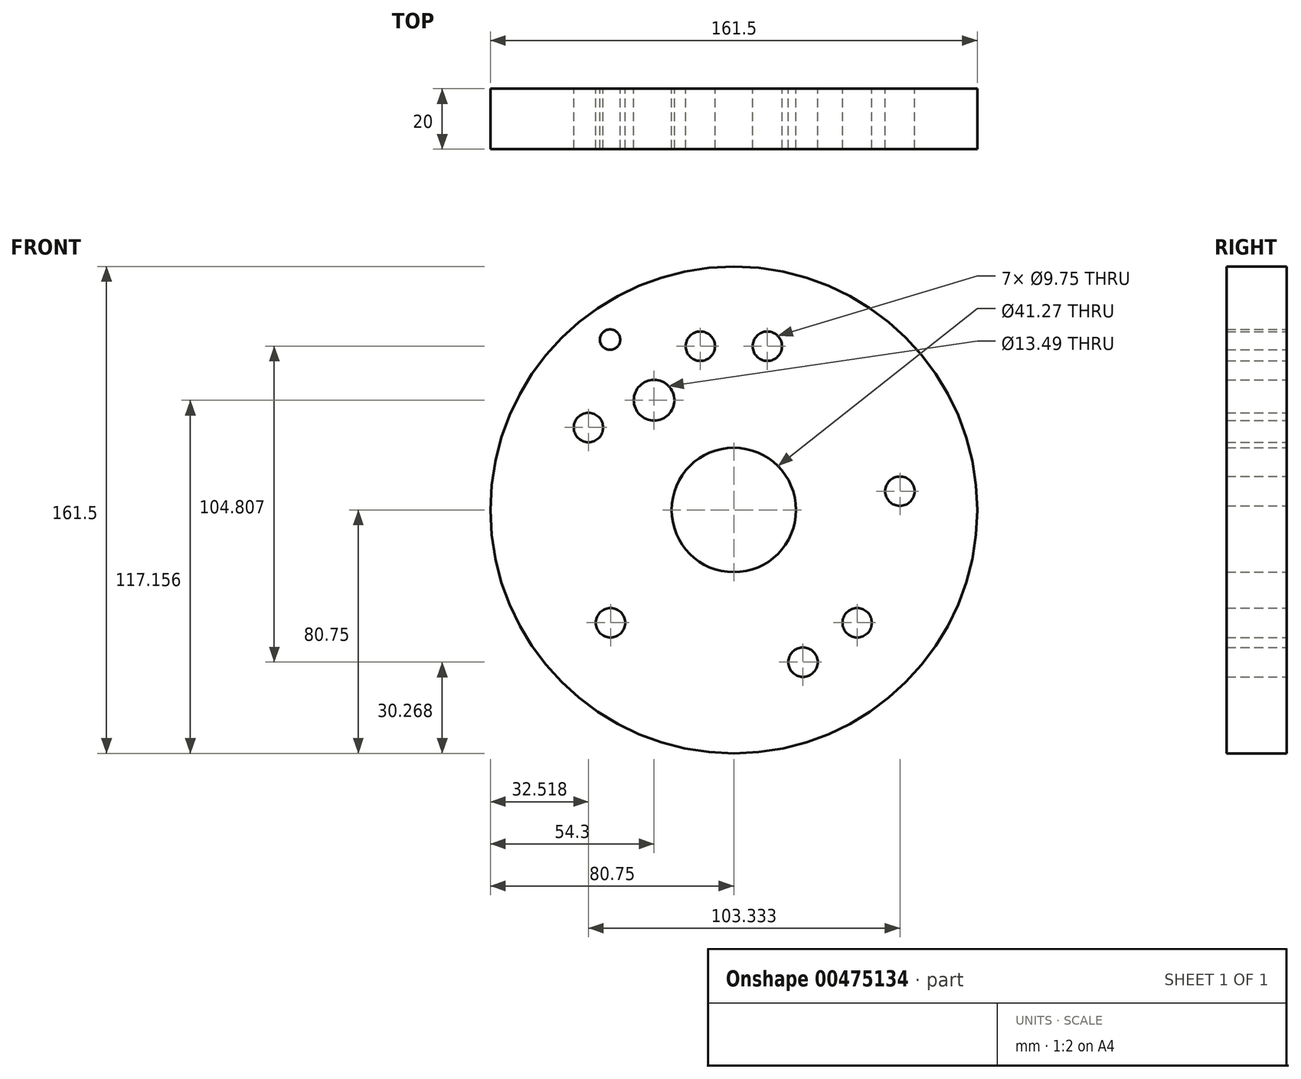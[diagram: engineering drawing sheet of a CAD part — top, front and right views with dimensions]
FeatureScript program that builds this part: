
annotation { "Feature Type Name" : "Feature", "Feature Type Description" : "" }
export const myFeature = defineFeature(function(context is Context, id is Id, definition is map)
    precondition{}
    {
        {
            var Q0;
            Q0=qCreatedBy(makeId("Front.planeOp"),FACE);
            var sketch = newSketch(context, id + "F0", { "sketchPlane" : qUnion([Q0])});
            skCircle(sketch, "E0", {"center": v(0, 0) * mm, "radius": 80.75 * mm});
            skCircle(sketch, "E1", {"center": v(0, 0) * mm, "radius": 20.64 * mm});
            skCircle(sketch, "E2", {"center": v(0, 0) * mm, "radius": 69.85 * mm, "construction": true});
            skLineSegment(sketch, "E3", {"start": v(-6.35, 61.72) * mm, "end": v(-6.35, 40.65) * mm, "construction": true});
            skLineSegment(sketch, "E4", {"start": v(-11.11, 61.72) * mm, "end": v(-11.11, 40.25) * mm, "construction": true});
            skCircle(sketch, "E5", {"center": v(-11.11, 54.33) * mm, "radius": 4.88 * mm});
            skLineSegment(sketch, "E6", {"start": v(0, 0) * mm, "end": v(-55.96, 77.02) * mm, "construction": true});
            skCircle(sketch, "E7.MirrorC", {"center": v(-48.23, 27.36) * mm, "radius": 4.88 * mm});
            skLineSegment(sketch, "E8.MirrorCS", {"start": v(-56.74, 25.11) * mm, "end": v(-36.7, 18.6) * mm, "construction": true});
            skCircle(sketch, "E9.1.0", {"center": v(-40.92, -37.42) * mm, "radius": 4.88 * mm});
            skCircle(sketch, "E9.1.1", {"center": v(-55.1, 6.22) * mm, "radius": 4.88 * mm});
            skCircle(sketch, "E9.2.0", {"center": v(22.94, -50.48) * mm, "radius": 4.88 * mm});
            skCircle(sketch, "E9.2.1", {"center": v(-22.94, -50.48) * mm, "radius": 4.88 * mm});
            skCircle(sketch, "E9.3.0", {"center": v(55.1, 6.22) * mm, "radius": 4.88 * mm});
            skCircle(sketch, "E9.3.1", {"center": v(40.92, -37.42) * mm, "radius": 4.88 * mm});
            skCircle(sketch, "E9.4.0", {"center": v(11.11, 54.33) * mm, "radius": 4.88 * mm});
            skCircle(sketch, "E9.4.1", {"center": v(48.23, 27.36) * mm, "radius": 4.88 * mm});
            skCircle(sketch, "E10", {"center": v(0, 0) * mm, "radius": 60.33 * mm, "construction": true});
            skCircle(sketch, "E11", {"center": v(0, 0) * mm, "radius": 45 * mm, "construction": true});
            skPoint(sketch, "E12", {"position": v(-26.45, 36.4) * mm});
            skPoint(sketch, "E13", {"position": v(-41.06, 56.5) * mm});
            skSolve(sketch);
        }
        {
            var Q0;
            Q0=makeQuery(id+"F0.imprint","IMPRINT",FACE,{"disambiguationData":[TD([[makeQuery(id+"F0.imprint","IMPRINT",EDGE,{"derivedFrom":sQuery(id+"F0.wireOp",EDGE,"E0")}),1.0]])]});
            var Q1;
            Q1=makeQuery(id+"F0.imprint","IMPRINT",FACE,{"disambiguationData":[TD([[makeQuery(id+"F0.imprint","IMPRINT",EDGE,{"derivedFrom":sQuery(id+"F0.wireOp",EDGE,"387447ca-5641-4527-8ccb-8136ee770e11.1.2.0")}),1.0]])]});
            var Q2;
            Q2=makeQuery(id+"F0.imprint","IMPRINT",FACE,{"disambiguationData":[TD([[makeQuery(id+"F0.imprint","IMPRINT",EDGE,{"derivedFrom":sQuery(id+"F0.wireOp",EDGE,"4ab3ce47-7b3f-4ca4-abf6-61af778339a8.1.1")}),-1.0]])]});
            var Q3;
            Q3=makeQuery(id+"F0.imprint","IMPRINT",FACE,{"disambiguationData":[TD([[makeQuery(id+"F0.imprint","IMPRINT",EDGE,{"derivedFrom":sQuery(id+"F0.wireOp",EDGE,"4ab3ce47-7b3f-4ca4-abf6-61af778339a8.1.0")}),1.0]])]});
            var Q4;
            Q4=makeQuery(id+"F0.imprint","IMPRINT",FACE,{"disambiguationData":[TD([[makeQuery(id+"F0.imprint","IMPRINT",EDGE,{"derivedFrom":sQuery(id+"F0.wireOp",EDGE,"387447ca-5641-4527-8ccb-8136ee770e11.2.3.0")}),-1.0]])]});
            var Q5;
            Q5=makeQuery(id+"F0.imprint","IMPRINT",FACE,{"disambiguationData":[TD([[makeQuery(id+"F0.imprint","IMPRINT",EDGE,{"derivedFrom":sQuery(id+"F0.wireOp",EDGE,"387447ca-5641-4527-8ccb-8136ee770e11.1.4.0")}),1.0]])]});
            var Q6;
            Q6=makeQuery(id+"F0.imprint","IMPRINT",FACE,{"disambiguationData":[TD([[makeQuery(id+"F0.imprint","IMPRINT",EDGE,{"derivedFrom":sQuery(id+"F0.wireOp",EDGE,"387447ca-5641-4527-8ccb-8136ee770e11.2.4.0")}),-1.0]])]});
            var Q7;
            Q7=makeQuery(id+"F0.imprint","IMPRINT",FACE,{"disambiguationData":[TD([[makeQuery(id+"F0.imprint","IMPRINT",EDGE,{"derivedFrom":sQuery(id+"F0.wireOp",EDGE,"E9.1.1")}),1.0]])]});
            var Q8;
            Q8=makeQuery(id+"F0.imprint","IMPRINT",FACE,{"disambiguationData":[TD([[makeQuery(id+"F0.imprint","IMPRINT",EDGE,{"derivedFrom":sQuery(id+"F0.wireOp",EDGE,"E9.1.0")}),-1.0]])]});
            var Q9;
            Q9=makeQuery(id+"F0.imprint","IMPRINT",FACE,{"disambiguationData":[TD([[makeQuery(id+"F0.imprint","IMPRINT",EDGE,{"derivedFrom":sQuery(id+"F0.wireOp",EDGE,"E9.2.1")}),1.0]])]});
            var Q10;
            Q10=makeQuery(id+"F0.imprint","IMPRINT",FACE,{"disambiguationData":[TD([[makeQuery(id+"F0.imprint","IMPRINT",EDGE,{"derivedFrom":sQuery(id+"F0.wireOp",EDGE,"E9.3.0")}),-1.0]])]});
            var Q11;
            Q11=makeQuery(id+"F0.imprint","IMPRINT",FACE,{"disambiguationData":[TD([[makeQuery(id+"F0.imprint","IMPRINT",EDGE,{"derivedFrom":sQuery(id+"F0.wireOp",EDGE,"E9.4.1")}),1.0]])]});
            var Q12;
            Q12=makeQuery(id+"F0.imprint","IMPRINT",FACE,{"disambiguationData":[TD([[makeQuery(id+"F0.imprint","IMPRINT",EDGE,{"derivedFrom":sQuery(id+"F0.wireOp",EDGE,"E9.4.0")}),-1.0]])]});
            extrude(context, id + "F1", {"entities" : qUnion([Q0, Q1, Q2, Q3, Q4, Q5, Q6, Q7, Q8, Q9, Q10, Q11, Q12]), "depth" : 20 * mm});
        }
        {
            var Q0;
            Q0=sQuery(id+"F0.wireOp",VERTEX,"E12");
            var Q1;
            Q1=makeQuery(id+"F1.opExtrude","SWEPT_BODY",BODY,{"disambiguationData":[OSD([sQuery(id+"F0.wireOp",EDGE,"E0"),sQuery(id+"F0.wireOp",EDGE,"E1"),sQuery(id+"F0.wireOp",EDGE,"E5"),sQuery(id+"F0.wireOp",EDGE,"E7.MirrorC"),sQuery(id+"F0.wireOp",EDGE,"E9.2.0"),sQuery(id+"F0.wireOp",EDGE,"E9.3.1")])]});
            hole(context, id + "F2", {"style" : HoleStyle.SIMPLE, "endStyle" : HoleEndStyle.THROUGH, "oppositeDirection" : true, "standardTappedOrClearance" : lookupTablePath({ "standard" : "ANSI", "fit" : "Normal (ASME)", "size" : "1/2", "type" : "Clearance" }), "standardBlindInLast" : lookupTablePath({ "fit" : "Free", "standard" : "ANSI", "size" : "1/2", "type" : "Clearance" }), "holeDiameter" : 13.5 * mm, "isTappedThrough" : true, "tappedDepth" : 12 * mm, "tapClearance" : 3, "startFromSketch" : true, "locations" : qUnion([Q0]), "scope" : qUnion([Q1])});
        }
        {
            var Q0;
            Q0=sQuery(id+"F0.wireOp",VERTEX,"E13");
            var Q1;
            Q1=makeQuery(id+"F1.opExtrude","SWEPT_BODY",BODY,{"disambiguationData":[OSD([sQuery(id+"F0.wireOp",EDGE,"E0"),sQuery(id+"F0.wireOp",EDGE,"E1"),sQuery(id+"F0.wireOp",EDGE,"E5"),sQuery(id+"F0.wireOp",EDGE,"E7.MirrorC"),sQuery(id+"F0.wireOp",EDGE,"E9.2.0"),sQuery(id+"F0.wireOp",EDGE,"E9.3.1")])]});
            hole(context, id + "F3", {"style" : HoleStyle.SIMPLE, "endStyle" : HoleEndStyle.THROUGH, "oppositeDirection" : true, "standardTappedOrClearance" : lookupTablePath({ "standard" : "ANSI", "fit" : "Normal (ASME)", "size" : "1/4", "type" : "Clearance" }), "standardBlindInLast" : lookupTablePath({ "fit" : "Free", "standard" : "ANSI", "size" : "1/4", "type" : "Clearance" }), "holeDiameter" : 6.76 * mm, "isTappedThrough" : true, "tappedDepth" : 12 * mm, "tapClearance" : 3, "startFromSketch" : true, "locations" : qUnion([Q0]), "scope" : qUnion([Q1])});
        }
    });
